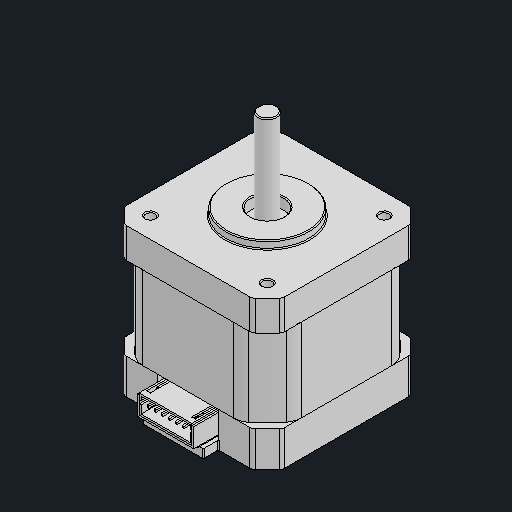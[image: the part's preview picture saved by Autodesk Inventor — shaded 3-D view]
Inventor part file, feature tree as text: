
AUTODESK INVENTOR PART (.ipt)
format: ipt  version: 2024.2 (Build 282272000, 272)  size: 423,936 bytes
history: native  units: mm
features: other x7, fillet x2, extrude x1
ambient origin geometry x8: Origin, YZ Plane, XZ Plane, XY Plane, X Axis, Y Axis, Z Axis, Center Point
bodies: Body1 (feature_tree), Body2 (feature_tree), Body3 (feature_tree), Body4 (feature_tree), Body5 (feature_tree)
feature tree (10):
  other  "솔리드1"
  other  "솔리드2"
  other  "솔리드3"
  other  "솔리드4"
  other  "솔리드5"
  fillet  "Fillet6"  [1 undecoded]
  fillet  "Fillet11"  [1 undecoded]
  extrude  "Extrude-Thin1"  [1 undecoded]
  other  "Boss-Extrude14"
  other  "Cut-Extrude11"
note: 3 required parameter values undecoded (feature->parameter linkage not recoverable at this tier; creation-order binding heuristic only, values carry confidence <= 0.55)
